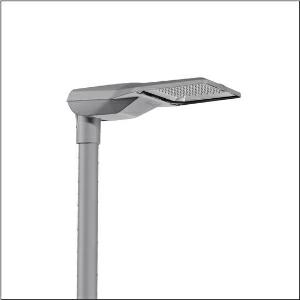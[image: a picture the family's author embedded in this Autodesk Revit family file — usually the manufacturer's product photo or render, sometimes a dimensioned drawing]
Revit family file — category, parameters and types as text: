
# Revit family: streetlight_sl_21_midi___st1_0a_5xe7d33a08mb_4240
name_source: partatom
category: Lighting Fixtures
units: mm (PartAtom-declared; Revit-internal decimal feet)

## family parameters
Cut with Voids When Loaded = No
Host = Face
Light Source = No
Part Type = Normal
Room Calculation Point = No
Round Connector Dimension = Use Diameter
Shared = No

## types (1)
- --- (1 x LED, 18270 lm, 136 W, 3000K)
    Apparent Load = 136 VA
    CIE Flux Codes = 37 72 97 100 100
    Color Rendering = 70
    Color Temperature = 3000K
    Default Elevation = 1800 mm
    Description = Streetlight SL 21 midi, mast luminaire, primary light control with lens, of PMMA, primary optical cover: cover, of toughened safety glass, transparent, light distribution: ST1.0a, light emission: direct distribution, primary light characteristic: asymmetric, installation type: post-top, side-entry, LED, 3G 1.5mm², High Power LED, rated luminous flux: 18.270lm, luminous efficacy: 134lm/W, light colour: 730, colour temperature: 3000K, control: flexible luminous flux parameterisation, time-dependent luminous flux control, constant luminous flux control, overheat protection, mains connection: 220..240V, AC, 50/60Hz, connection cable pre-assembled, cable length: 12,5m, wiring characteristics: H07RN-F, start of lifetime: 136W, end of service life: 142W, reduction: 61W, luminaire housing, of diecast aluminium, powder-coated, Siteco® metallic grey (DB 702S), corrosivity category C5 mid according to DIN EN ISO 12944, please order mast flange separately, inclination adjustable: 0°, 5°, 10°, 15°, sealing non-destructively replaceable, multi-level sealing system, length: 644mm, width: 335mm, height: 110mm, mast flange for spigot size: 42mm (side-entry): 5XC10008XM4, 60/48mm (side-entry/post-top): 5XC10108XM2, 76/60mm (side-entry/post-top): 5XC10108XM1, protection rating (complete): IP66, insulation class (complete): insulation class II (safety insulation), certification: CE, ENEC, ENEC+, VDE, impact resistance: IK09, permissible operating ambient temperature for outdoor applications: -40..+50°C, standard-compliant lighting for roads and squares, packaging unit: 1 piece

Light Distribution: ST1.0a
    Height = 111 mm
    Lamp = 1 x LED
    Lamp Light Flux = 18270 lm
    Lamp Power = 136 W
    Lamp count = 1
    Length = 644 mm
    Luminous efficacy = 134 lm/W
    Manufacturer = Siteco
    ModVariant = No
    Model = 5XE7D33A08MB
    Number of Poles = 1
    OnlyDefault = Yes
    Power Factor = 1
    Product Name = Streetlight SL 21 midi | ST1.0a
    Product group = mast luminaire | pylon top
    ProductGroupID = 6100
    Protection Class = Protection class II
    Protection Degree = IP 66
    RLX_Detail_Level = 1
    RLX_Emergency_Light_Flux = 0 lm
    RLX_Emergency_Type = 0
    RLX_Emergency_Type_DB = No
    RlxData = <blob elided: 89989 chars, md5=f8435b96>
    Socket = socket
    Standby Power = 0 W
    System Light Flux = 18270 lm
    System Power = 136 W
    Type Comments = factory setting: luminous flux: 100 % | Output Level: 100 % | 695 mA
    Type Image = l_1004298.jpg
    URL = http://relux.com
    VarID = @adj_141089
    Voltage = 0 V
    Weight = 0.00 kg
    Width = 336 mm

## geometry (parser evidence)
native form markers: Blend x4, Sweep x11
no freeform markers — native parametric forms only
